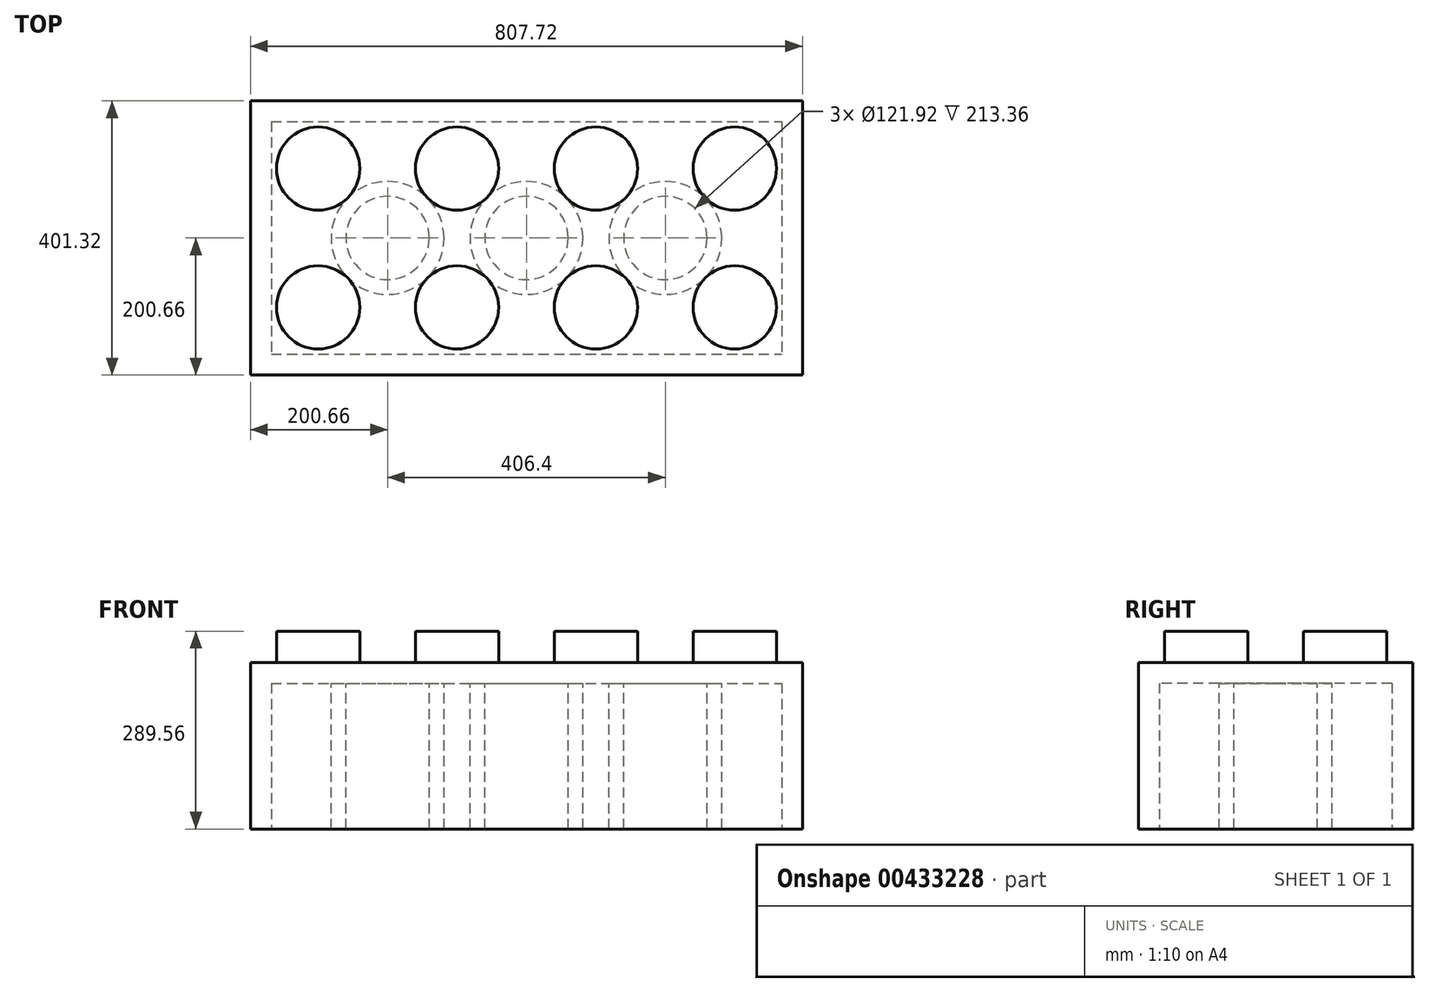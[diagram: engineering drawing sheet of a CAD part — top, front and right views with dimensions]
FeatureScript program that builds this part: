
annotation { "Feature Type Name" : "Feature", "Feature Type Description" : "" }
export const myFeature = defineFeature(function(context is Context, id is Id, definition is map)
    precondition{}
    {
        {
            var Q0;
            Q0=qCreatedBy(makeId("Top.planeOp"),FACE);
            var sketch = newSketch(context, id + "F0", { "sketchPlane" : qUnion([Q0])});
            skLineSegment(sketch, "E0.bottom", {"start": v(0, 0) * mm, "end": v(-807.72, 0) * mm});
            skLineSegment(sketch, "E0.top", {"start": v(0, 401.32) * mm, "end": v(-807.72, 401.32) * mm});
            skLineSegment(sketch, "E0.left", {"start": v(0, 0) * mm, "end": v(0, 401.32) * mm});
            skLineSegment(sketch, "E0.right", {"start": v(-807.72, 0) * mm, "end": v(-807.72, 401.32) * mm});
            skSolve(sketch);
        }
        {
            var Q0;
            Q0=makeQuery(id+"F0.imprint","IMPRINT",FACE,{"disambiguationData":[TD([[makeQuery(id+"F0.imprint","IMPRINT",EDGE,{"derivedFrom":sQuery(id+"F0.wireOp",EDGE,"E0.bottom")}),-1.0]])]});
            extrude(context, id + "F1", {"entities" : qUnion([Q0]), "depth" : 243.84 * mm});
        }
        {
            var Q0;
            Q0=makeQuery(id+"F1.opExtrude","CAP_FACE",FACE,{"disambiguationData":[OSD([sQuery(id+"F0.wireOp",EDGE,"E0.bottom"),sQuery(id+"F0.wireOp",EDGE,"E0.top"),sQuery(id+"F0.wireOp",EDGE,"E0.left"),sQuery(id+"F0.wireOp",EDGE,"E0.right")])],"isStart":false});
            var sketch = newSketch(context, id + "F2", { "sketchPlane" : qUnion([Q0])});
            skCircle(sketch, "E1", {"center": v(-708.66, 302.26) * mm, "radius": 60.96 * mm});
            skCircle(sketch, "E2.0.1.0", {"center": v(-708.66, 99.06) * mm, "radius": 60.96 * mm});
            skCircle(sketch, "E2.1.0.0", {"center": v(-505.46, 302.26) * mm, "radius": 60.96 * mm});
            skCircle(sketch, "E2.1.1.0", {"center": v(-505.46, 99.06) * mm, "radius": 60.96 * mm});
            skCircle(sketch, "E2.2.0.0", {"center": v(-302.26, 302.26) * mm, "radius": 60.96 * mm});
            skCircle(sketch, "E2.2.1.0", {"center": v(-302.26, 99.06) * mm, "radius": 60.96 * mm});
            skCircle(sketch, "E2.3.0.0", {"center": v(-99.06, 302.26) * mm, "radius": 60.96 * mm});
            skCircle(sketch, "E2.3.1.0", {"center": v(-99.06, 99.06) * mm, "radius": 60.96 * mm});
            skLineSegment(sketch, "E2.direction1", {"start": v(-708.66, 302.26) * mm, "end": v(-505.46, 302.26) * mm, "construction": true});
            skLineSegment(sketch, "E2.direction2", {"start": v(-708.66, 302.26) * mm, "end": v(-708.66, 99.06) * mm, "construction": true});
            skSolve(sketch);
        }
        {
            var Q0;
            Q0=makeQuery(id+"F2.imprint","IMPRINT",FACE,{"disambiguationData":[TD([[makeQuery(id+"F2.imprint","IMPRINT",EDGE,{"derivedFrom":sQuery(id+"F2.wireOp",EDGE,"E1")}),1.0]])]});
            var Q1;
            Q1=makeQuery(id+"F2.imprint","IMPRINT",FACE,{"disambiguationData":[TD([[makeQuery(id+"F2.imprint","IMPRINT",EDGE,{"derivedFrom":sQuery(id+"F2.wireOp",EDGE,"E2.1.0.0")}),1.0]])]});
            var Q2;
            Q2=makeQuery(id+"F2.imprint","IMPRINT",FACE,{"disambiguationData":[TD([[makeQuery(id+"F2.imprint","IMPRINT",EDGE,{"derivedFrom":sQuery(id+"F2.wireOp",EDGE,"E2.2.0.0")}),1.0]])]});
            var Q3;
            Q3=makeQuery(id+"F2.imprint","IMPRINT",FACE,{"disambiguationData":[TD([[makeQuery(id+"F2.imprint","IMPRINT",EDGE,{"derivedFrom":sQuery(id+"F2.wireOp",EDGE,"E2.3.0.0")}),1.0]])]});
            var Q4;
            Q4=makeQuery(id+"F2.imprint","IMPRINT",FACE,{"disambiguationData":[TD([[makeQuery(id+"F2.imprint","IMPRINT",EDGE,{"derivedFrom":sQuery(id+"F2.wireOp",EDGE,"E2.3.1.0")}),1.0]])]});
            var Q5;
            Q5=makeQuery(id+"F2.imprint","IMPRINT",FACE,{"disambiguationData":[TD([[makeQuery(id+"F2.imprint","IMPRINT",EDGE,{"derivedFrom":sQuery(id+"F2.wireOp",EDGE,"E2.2.1.0")}),1.0]])]});
            var Q6;
            Q6=makeQuery(id+"F2.imprint","IMPRINT",FACE,{"disambiguationData":[TD([[makeQuery(id+"F2.imprint","IMPRINT",EDGE,{"derivedFrom":sQuery(id+"F2.wireOp",EDGE,"E2.1.1.0")}),1.0]])]});
            var Q7;
            Q7=makeQuery(id+"F2.imprint","IMPRINT",FACE,{"disambiguationData":[TD([[makeQuery(id+"F2.imprint","IMPRINT",EDGE,{"derivedFrom":sQuery(id+"F2.wireOp",EDGE,"E2.0.1.0")}),1.0]])]});
            extrude(context, id + "F3", {"entities" : qUnion([Q0, Q1, Q2, Q3, Q4, Q5, Q6, Q7]), "operationType" : NewBodyOperationType.ADD, "depth" : 45.72 * mm});
        }
        {
            var Q0;
            Q0=makeQuery(id+"F1.opExtrude","CAP_FACE",FACE,{"disambiguationData":[OSD([sQuery(id+"F0.wireOp",EDGE,"E0.bottom"),sQuery(id+"F0.wireOp",EDGE,"E0.top"),sQuery(id+"F0.wireOp",EDGE,"E0.left"),sQuery(id+"F0.wireOp",EDGE,"E0.right")])],"isStart":true});
            var sketch = newSketch(context, id + "F4", { "sketchPlane" : qUnion([Q0])});
            skLineSegment(sketch, "E3.bottom", {"start": v(-777.24, -370.84) * mm, "end": v(-30.48, -370.84) * mm});
            skLineSegment(sketch, "E3.top", {"start": v(-777.24, -30.48) * mm, "end": v(-30.48, -30.48) * mm});
            skLineSegment(sketch, "E3.left", {"start": v(-777.24, -370.84) * mm, "end": v(-777.24, -30.48) * mm});
            skLineSegment(sketch, "E3.right", {"start": v(-30.48, -370.84) * mm, "end": v(-30.48, -30.48) * mm});
            skSolve(sketch);
        }
        {
            var Q0;
            Q0=makeQuery(id+"F4.imprint","IMPRINT",FACE,{"disambiguationData":[TD([[makeQuery(id+"F4.imprint","IMPRINT",EDGE,{"derivedFrom":sQuery(id+"F4.wireOp",EDGE,"E3.bottom")}),1.0]])]});
            extrude(context, id + "F5", {"entities" : qUnion([Q0]), "operationType" : NewBodyOperationType.REMOVE, "oppositeDirection" : true, "depth" : 213.36 * mm});
        }
        {
            var Q0;
            Q0=makeQuery(id+"F5.boolean.opBoolean","COPY",FACE,{"derivedFrom":makeQuery(id+"F5.opExtrude","CAP_FACE",FACE,{"disambiguationData":[OSD([sQuery(id+"F4.wireOp",EDGE,"E3.bottom"),sQuery(id+"F4.wireOp",EDGE,"E3.top"),sQuery(id+"F4.wireOp",EDGE,"E3.left"),sQuery(id+"F4.wireOp",EDGE,"E3.right")])],"isStart":false})});
            var sketch = newSketch(context, id + "F6", { "sketchPlane" : qUnion([Q0])});
            skCircle(sketch, "E4", {"center": v(-403.86, -200.66) * mm, "radius": 82.55 * mm});
            skCircle(sketch, "E5", {"center": v(-403.86, -200.66) * mm, "radius": 60.96 * mm});
            skCircle(sketch, "E6.1.0.0", {"center": v(-200.66, -200.66) * mm, "radius": 60.96 * mm});
            skCircle(sketch, "E6.1.0.1", {"center": v(-200.66, -200.66) * mm, "radius": 82.55 * mm});
            skLineSegment(sketch, "E6.direction1", {"start": v(-403.86, -200.66) * mm, "end": v(-200.66, -200.66) * mm, "construction": true});
            skCircle(sketch, "E7.1.0.0", {"center": v(-607.06, -200.66) * mm, "radius": 60.96 * mm});
            skCircle(sketch, "E7.1.0.1", {"center": v(-607.06, -200.66) * mm, "radius": 82.55 * mm});
            skLineSegment(sketch, "E7.direction1", {"start": v(-403.86, -200.66) * mm, "end": v(-607.06, -200.66) * mm, "construction": true});
            skSolve(sketch);
        }
        {
            var Q0;
            Q0=makeQuery(id+"F6.imprint","IMPRINT",FACE,{"disambiguationData":[TD([[makeQuery(id+"F6.imprint","IMPRINT",EDGE,{"derivedFrom":sQuery(id+"F6.wireOp",EDGE,"E7.1.0.0")}),-1.0]])]});
            var Q1;
            Q1=makeQuery(id+"F6.imprint","IMPRINT",FACE,{"disambiguationData":[TD([[makeQuery(id+"F6.imprint","IMPRINT",EDGE,{"derivedFrom":sQuery(id+"F6.wireOp",EDGE,"E4")}),1.0]])]});
            var Q2;
            Q2=makeQuery(id+"F6.imprint","IMPRINT",FACE,{"disambiguationData":[TD([[makeQuery(id+"F6.imprint","IMPRINT",EDGE,{"derivedFrom":sQuery(id+"F6.wireOp",EDGE,"E6.1.0.0")}),-1.0]])]});
            extrude(context, id + "F7", {"entities" : qUnion([Q0, Q1, Q2]), "operationType" : NewBodyOperationType.ADD, "depth" : 213.36 * mm});
        }
        {
            var Q0;
            Q0=makeQuery(id+"F1.opExtrude","SWEPT_BODY",BODY,{"disambiguationData":[OSD([sQuery(id+"F0.wireOp",EDGE,"E0.bottom"),sQuery(id+"F0.wireOp",EDGE,"E0.top"),sQuery(id+"F0.wireOp",EDGE,"E0.left"),sQuery(id+"F0.wireOp",EDGE,"E0.right")])]});
            transform(context, id + "F8", {"entities" : qUnion([Q0]), "transformType" : TransformType.TRANSLATION_3D, "dx" : 0 * mm, "dy" : 0 * mm, "dz" : 0 * mm, "makeCopy" : true});
        }
        {
            var Q0;
            Q0=makeQuery(id+"F8.opPattern","COPY",BODY,{"derivedFrom":makeQuery(id+"F1.opExtrude","SWEPT_BODY",BODY,{"disambiguationData":[OSD([sQuery(id+"F0.wireOp",EDGE,"E0.bottom"),sQuery(id+"F0.wireOp",EDGE,"E0.top"),sQuery(id+"F0.wireOp",EDGE,"E0.left"),sQuery(id+"F0.wireOp",EDGE,"E0.right")])]}),"instanceName":"1"});
            deleteBodies(context, id + "F9", {"entities" : qUnion([Q0])});
        }
        {
            var Q0;
            Q0=makeQuery(id+"F1.opExtrude","SWEPT_BODY",BODY,{"disambiguationData":[OSD([sQuery(id+"F0.wireOp",EDGE,"E0.bottom"),sQuery(id+"F0.wireOp",EDGE,"E0.top"),sQuery(id+"F0.wireOp",EDGE,"E0.left"),sQuery(id+"F0.wireOp",EDGE,"E0.right")])]});
            transform(context, id + "F10", {"entities" : qUnion([Q0]), "transformType" : TransformType.TRANSLATION_3D, "dx" : 0 * mm, "dy" : 0 * mm, "dz" : 0 * mm, "makeCopy" : true});
        }
        {
            var Q0;
            Q0=makeQuery(id+"F10.opPattern","COPY",BODY,{"derivedFrom":makeQuery(id+"F1.opExtrude","SWEPT_BODY",BODY,{"disambiguationData":[OSD([sQuery(id+"F0.wireOp",EDGE,"E0.bottom"),sQuery(id+"F0.wireOp",EDGE,"E0.top"),sQuery(id+"F0.wireOp",EDGE,"E0.left"),sQuery(id+"F0.wireOp",EDGE,"E0.right")])]}),"instanceName":"1"});
            deleteBodies(context, id + "F11", {"entities" : qUnion([Q0])});
        }
    });
